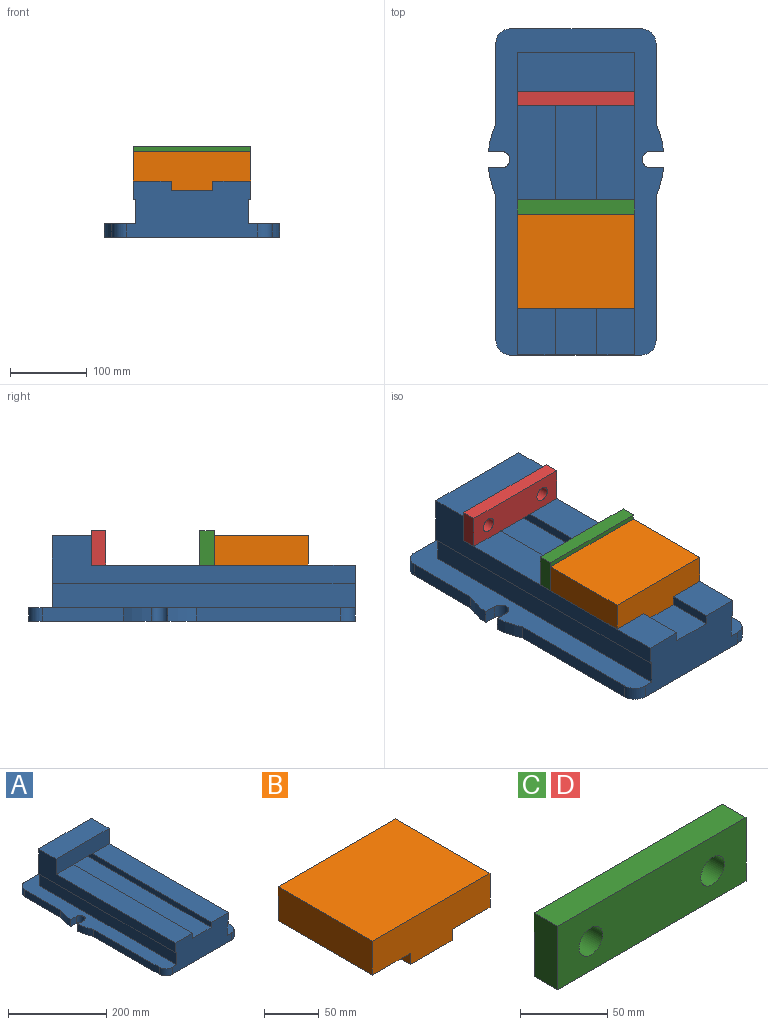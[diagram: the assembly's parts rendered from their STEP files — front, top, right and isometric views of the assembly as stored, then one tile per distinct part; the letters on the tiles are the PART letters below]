
ASSEMBLY  parts=4 mates=6
PART A: 37 faces, bbox 227.6x423.9x111.1 mm
  f0: plane 187.5x17.46mm, normal (1,0,0), area 3274.3mm2, adj f1,f18,f19,f21
  f1: cylinder r=114.3mm len=36.77mm, axis (0,0,-1), area 667.7mm2, adj f0,f2,f18,f21
  f2: plane 17.46x16.96mm, normal (0,1,0), area 296.2mm2, adj f1,f3,f18,f21
  f3: cylinder r=10.67mm len=21.35mm, axis (0,0,-1), area 585.5mm2, adj f2,f4,f18,f21
  f4: plane 17.46x16.96mm, normal (0,-1,0), area 296.2mm2, adj f3,f5,f18,f21
  f5: cylinder r=114.3mm len=36.77mm, axis (0,0,-1), area 667.7mm2, adj f4,f6,f18,f21
  f6: plane 103.37x17.46mm, normal (1,0,0), area 1805mm2, adj f5,f7,f18,f21
  f7: cylinder r=19.05mm len=19.05mm, axis (0,0,-1), area 522.5mm2, adj f6,f8,f18,f21
  f8: plane 171.12x17.46mm, normal (0,1,0), area 2988.2mm2, adj f7,f9,f18,f21
  f9: cylinder r=17.81mm len=17.81mm, axis (0,0,-1), area 488.4mm2, adj f8,f10,f18,f21
  f10: plane 104.61x17.46mm, normal (-1,0,0), area 1826.8mm2, adj f9,f11,f18,f21
  f11: cylinder r=114.3mm len=36.77mm, axis (0,0,-1), area 667.7mm2, adj f10,f12,f18,f21
  f12: plane 17.46x16.96mm, normal (0,-1,0), area 296.2mm2, adj f11,f13,f18,f21
  f13: cylinder r=10.67mm len=21.35mm, axis (0,0,-1), area 585.5mm2, adj f12,f14,f18,f21
  f14: plane 17.46x16.96mm, normal (0,1,0), area 296.2mm2, adj f13,f15,f18,f21
  f15: cylinder r=114.3mm len=36.77mm, axis (0,0,-1), area 667.7mm2, adj f14,f16,f18,f21
  f16: plane 187.5x17.46mm, normal (-1,0,0), area 3274.3mm2, adj f15,f17,f18,f21
  f17: cylinder r=19.05mm len=19.05mm, axis (0,0,-1), area 522.5mm2, adj f16,f18,f21,f27
  f18: plane 423.86x227.6mm, normal (0,0,-1), area 88071.8mm2, adj f0,f1,f2,f3,f4,f5,f6,f7
  f19: cylinder r=19.05mm len=19.05mm, axis (0,0,-1), area 522.5mm2, adj f0,f18,f21,f27
  f20: plane 393.7x31.75mm, normal (1,0,0), area 12500mm2, adj f21,f27,f28,f29
  f21: plane 423.86x227.6mm, normal (0,0,1), area 30572mm2, adj f0,f1,f2,f3,f4,f5,f6,f7
  f22: plane 393.7x31.75mm, normal (-1,0,0), area 12500mm2, adj f21,f24,f27,f29
  f23: plane 393.7x53.98mm, normal (0,0,1), area 21250mm2, adj f25,f26,f27,f29
  f24: plane 393.7x3.18mm, normal (0,0,-1), area 1250mm2, adj f22,f27,f29,f31
  f25: plane 393.7x12.7mm, normal (1,0,0), area 5000mm2, adj f23,f27,f29,f32,f33
  f26: plane 393.7x12.7mm, normal (-1,0,0), area 5000mm2, adj f23,f27,f29,f33,f34
  f27: plane 169.88x73.03mm, normal (0,-1,0), area 10547.1mm2, adj f17,f18,f19,f20,f21,f22,f23,f24
  f28: plane 393.7x3.18mm, normal (0,0,-1), area 1250mm2, adj f20,f27,f29,f35
  f29: plane 152.4x93.66mm, normal (0,1,0), area 13387.1mm2, adj f20,f21,f22,f23,f24,f25,f26,f28
  f30: plane 152.4x50.8mm, normal (0,0,1), area 7741.9mm2, adj f29,f31,f35,f36
  f31: plane 393.7x61.91mm, normal (-1,0,0), area 11310.5mm2, adj f24,f27,f29,f30,f32,f36
  f32: plane 342.9x49.21mm, normal (0,0,1), area 16875mm2, adj f25,f27,f31,f36
  f33: plane 53.98x50.8mm, normal (0,0,-1), area 2741.9mm2, adj f25,f26,f29,f36
  f34: plane 342.9x49.21mm, normal (0,0,1), area 16875mm2, adj f26,f27,f35,f36
  f35: plane 393.7x61.91mm, normal (1,0,0), area 11310.5mm2, adj f27,f28,f29,f30,f34,f36
  f36: plane 152.4x38.1mm, normal (0,-1,0), area 5806.4mm2, adj f30,f31,f32,f33,f34,f35
PART B: 10 faces, bbox 152.4x122.2x50.8 mm
  f0: plane 152.4x122.24mm, normal (0,0,1), area 18629mm2, adj f1,f4,f6,f8
  f1: plane 122.24x38.1mm, normal (1,0,0), area 4657.2mm2, adj f0,f2,f6,f8
  f2: plane 122.24x49.21mm, normal (0,0,-1), area 6015.6mm2, adj f1,f3,f6,f8
  f3: plane 122.24x12.7mm, normal (1,0,0), area 1552.4mm2, adj f2,f5,f6,f8
  f4: plane 122.24x38.1mm, normal (-1,0,0), area 4657.2mm2, adj f0,f6,f7,f8
  f5: plane 122.24x53.98mm, normal (0,0,-1), area 6597.8mm2, adj f3,f6,f8,f9
  f6: plane 152.4x50.8mm, normal (0,-1,0), area 6491.9mm2, adj f0,f1,f2,f3,f4,f5,f7,f9
  f7: plane 122.24x49.21mm, normal (0,0,-1), area 6015.6mm2, adj f4,f6,f8,f9
  f8: plane 152.4x50.8mm, normal (0,1,0), area 6491.9mm2, adj f0,f1,f2,f3,f4,f5,f7,f9
  f9: plane 122.24x12.7mm, normal (-1,0,0), area 1552.4mm2, adj f5,f6,f7,f8
PART C: 8 faces, bbox 152.4x19.1x44.5 mm
  f0: cylinder r=9.53mm len=19.05mm, axis (0,1,0), area 1140.1mm2, adj f3,f5
  f1: cylinder r=9.53mm len=19.05mm, axis (0,1,0), area 1140.1mm2, adj f3,f5
  f2: plane 152.4x19.05mm, normal (0,0,1), area 2903.2mm2, adj f3,f4,f5,f6
  f3: plane 152.4x44.45mm, normal (0,1,0), area 6204.1mm2, adj f0,f1,f2,f4,f6,f7
  f4: plane 44.45x19.05mm, normal (1,0,0), area 846.8mm2, adj f2,f3,f5,f7
  f5: plane 152.4x44.45mm, normal (0,-1,0), area 6204.1mm2, adj f0,f1,f2,f4,f6,f7
  f6: plane 44.45x19.05mm, normal (-1,0,0), area 846.8mm2, adj f2,f3,f5,f7
  f7: plane 152.4x19.05mm, normal (0,0,-1), area 2903.2mm2, adj f3,f4,f5,f6
PART D: same geometry as C
PLACE A t=(0,-146.05,-61.91)mm
PLACE B t=(0,-160.05,-38.1)mm
PLACE C t=(0,-150.53,-38.1)mm
PLACE D t=(0,-9.53,-38.1)mm
MATE planar A.f35 <-> C.f4  axis (1,0,0) through (76.2,-116.71,-44.71)mm
MATE planar C.f5 <-> B.f8  axis (0,-1,0) through (0,-160.05,-15.73)mm
MATE planar C.f7 <-> A.f34  axis (0,0,-1) through (0,-150.53,-38.1)mm
MATE planar A.f32 <-> B.f7  axis (0,0,1) through (-51.59,-171.45,-38.1)mm
MATE fastened D.f7 <-> A.f33  axis (0,0,1) through (0,0,-38.1)mm
MATE planar B.f3 <-> A.f26  axis (1,0,0) through (26.99,-221.17,-44.45)mm
